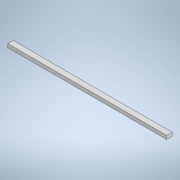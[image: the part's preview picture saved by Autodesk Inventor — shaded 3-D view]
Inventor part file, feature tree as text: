
AUTODESK INVENTOR PART (.ipt)
format: ipt  version: 2021 (Build 250183000, 183)  size: 93,184 bytes
history: native  units: mm
features: extrude x1, sketch x1
ambient origin geometry x8: Origin, YZ Plane, XZ Plane, XY Plane, X Axis, Y Axis, Z Axis, Center Point
bodies: Solid1 (feature_tree)
feature tree (2):
  extrude  "Extrusion1"  Depth=8.0mm
  sketch  "Sketch1"  dims[d0=12.0mm d1=8.0mm d2=350.0mm d3=0.0mm]
